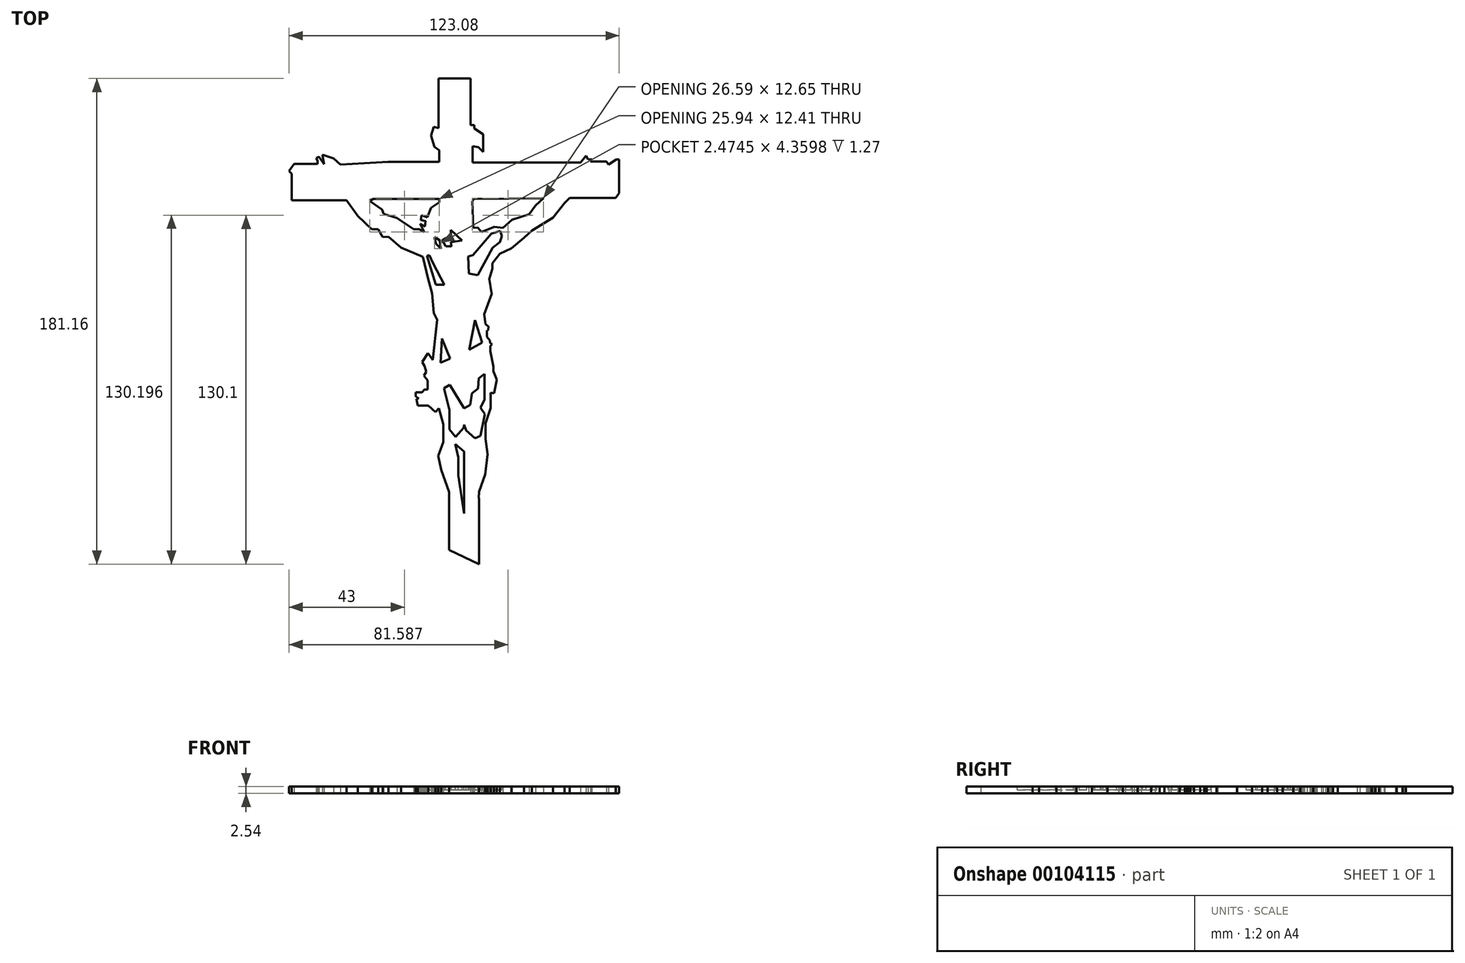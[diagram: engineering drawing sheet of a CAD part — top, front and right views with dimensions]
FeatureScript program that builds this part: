
annotation { "Feature Type Name" : "Feature", "Feature Type Description" : "" }
export const myFeature = defineFeature(function(context is Context, id is Id, definition is map)
    precondition{}
    {
        {
            var Q0;
            Q0=qCreatedBy(makeId("Top.planeOp"),FACE);
            var sketch = newSketch(context, id + "F0", { "sketchPlane" : qUnion([Q0])});
            skLineSegment(sketch, "E0", {"start": v(-9.57, 83.57) * mm, "end": v(-6, 83.57) * mm});
            skLineSegment(sketch, "E1", {"start": v(-6, 83.57) * mm, "end": v(-2.71, 83.57) * mm});
            skLineSegment(sketch, "E2", {"start": v(-2.71, 83.57) * mm, "end": v(1.86, 83.57) * mm});
            skLineSegment(sketch, "E3", {"start": v(1.86, 83.57) * mm, "end": v(2.48, 83.57) * mm});
            skLineSegment(sketch, "E4", {"start": v(2.48, 83.57) * mm, "end": v(2.48, 74.86) * mm});
            skLineSegment(sketch, "E5", {"start": v(2.48, 74.86) * mm, "end": v(2.48, 66.25) * mm});
            skLineSegment(sketch, "E6", {"start": v(2.48, 66.25) * mm, "end": v(3.84, 66.25) * mm});
            skLineSegment(sketch, "E7", {"start": v(3.14, 58.38) * mm, "end": v(3.14, 52.19) * mm});
            skLineSegment(sketch, "E8", {"start": v(3.14, 52.19) * mm, "end": v(24.8, 52.19) * mm});
            skLineSegment(sketch, "E9", {"start": v(24.8, 52.19) * mm, "end": v(43.45, 52.19) * mm});
            skLineSegment(sketch, "E10", {"start": v(47.37, 52.57) * mm, "end": v(53.14, 52.57) * mm});
            skLineSegment(sketch, "E11", {"start": v(53.14, 52.57) * mm, "end": v(53.88, 51.45) * mm});
            skLineSegment(sketch, "E12", {"start": v(53.88, 51.45) * mm, "end": v(56.77, 53.38) * mm});
            skLineSegment(sketch, "E13", {"start": v(56.77, 53.38) * mm, "end": v(57.85, 53.38) * mm});
            skLineSegment(sketch, "E14", {"start": v(57.85, 53.38) * mm, "end": v(57.85, 40.79) * mm});
            skLineSegment(sketch, "E15", {"start": v(57.85, 40.79) * mm, "end": v(56.55, 38.99) * mm});
            skLineSegment(sketch, "E16", {"start": v(56.55, 38.99) * mm, "end": v(39.44, 38.99) * mm});
            skLineSegment(sketch, "E17", {"start": v(29.65, 38.93) * mm, "end": v(3.69, 38.7) * mm});
            skLineSegment(sketch, "E18", {"start": v(3.69, 38.7) * mm, "end": v(3.06, 37.74) * mm});
            skLineSegment(sketch, "E19", {"start": v(3.06, 37.74) * mm, "end": v(3.47, 27.88) * mm});
            skLineSegment(sketch, "E20", {"start": v(3.47, 27.88) * mm, "end": v(5.04, 27.94) * mm});
            skLineSegment(sketch, "E21", {"start": v(5.04, 27.94) * mm, "end": v(6.46, 26.28) * mm});
            skLineSegment(sketch, "E22", {"start": v(6.46, 26.28) * mm, "end": v(11.34, 28.3) * mm});
            skLineSegment(sketch, "E23", {"start": v(11.34, 28.3) * mm, "end": v(14.45, 27.88) * mm});
            skLineSegment(sketch, "E24", {"start": v(14.45, 27.88) * mm, "end": v(17.99, 30.92) * mm});
            skLineSegment(sketch, "E25", {"start": v(17.99, 30.92) * mm, "end": v(24.26, 32.96) * mm});
            skLineSegment(sketch, "E26", {"start": v(24.26, 32.96) * mm, "end": v(26.65, 36.24) * mm});
            skLineSegment(sketch, "E27", {"start": v(26.65, 36.24) * mm, "end": v(29.65, 38.93) * mm});
            skLineSegment(sketch, "E28", {"start": v(39.44, 38.99) * mm, "end": v(37.47, 37.1) * mm});
            skLineSegment(sketch, "E29", {"start": v(37.47, 37.1) * mm, "end": v(33.12, 31.64) * mm});
            skLineSegment(sketch, "E30", {"start": v(33.12, 31.64) * mm, "end": v(25.33, 26.87) * mm});
            skLineSegment(sketch, "E31", {"start": v(25.33, 26.87) * mm, "end": v(22.33, 24.19) * mm});
            skLineSegment(sketch, "E32", {"start": v(22.33, 24.19) * mm, "end": v(17.66, 20.26) * mm});
            skLineSegment(sketch, "E33", {"start": v(17.66, 20.26) * mm, "end": v(13.41, 18.17) * mm});
            skLineSegment(sketch, "E34", {"start": v(13.41, 18.17) * mm, "end": v(10.56, 14.7) * mm});
            skLineSegment(sketch, "E35", {"start": v(10.56, 14.7) * mm, "end": v(10.56, 12.67) * mm});
            skLineSegment(sketch, "E36", {"start": v(10.56, 12.67) * mm, "end": v(9.45, 8.78) * mm});
            skLineSegment(sketch, "E37", {"start": v(9.45, 8.78) * mm, "end": v(10.35, 3.2) * mm});
            skLineSegment(sketch, "E38", {"start": v(10.35, 3.2) * mm, "end": v(7.5, -4.35) * mm});
            skLineSegment(sketch, "E39", {"start": v(7.5, -4.35) * mm, "end": v(8, -8.1) * mm});
            skLineSegment(sketch, "E40", {"start": v(8, -8.1) * mm, "end": v(9.18, -9.02) * mm});
            skLineSegment(sketch, "E41", {"start": v(9.18, -9.02) * mm, "end": v(8.97, -10.46) * mm});
            skLineSegment(sketch, "E42", {"start": v(8.97, -10.46) * mm, "end": v(8.53, -10.4) * mm});
            skLineSegment(sketch, "E43", {"start": v(8.53, -10.4) * mm, "end": v(8.53, -12.78) * mm});
            skLineSegment(sketch, "E44", {"start": v(8.53, -12.78) * mm, "end": v(9.67, -14.22) * mm});
            skLineSegment(sketch, "E45", {"start": v(9.67, -14.22) * mm, "end": v(9.67, -14.96) * mm});
            skLineSegment(sketch, "E46", {"start": v(9.67, -14.96) * mm, "end": v(10.4, -15.53) * mm});
            skLineSegment(sketch, "E47", {"start": v(10.4, -15.53) * mm, "end": v(9.86, -16.26) * mm});
            skLineSegment(sketch, "E48", {"start": v(9.86, -16.26) * mm, "end": v(9.86, -18.07) * mm});
            skLineSegment(sketch, "E49", {"start": v(9.86, -18.07) * mm, "end": v(11, -23.8) * mm});
            skLineSegment(sketch, "E50", {"start": v(11, -23.8) * mm, "end": v(11, -25.56) * mm});
            skLineSegment(sketch, "E51", {"start": v(11, -25.56) * mm, "end": v(12.16, -28.82) * mm});
            skLineSegment(sketch, "E52", {"start": v(12.16, -28.82) * mm, "end": v(11.23, -33.84) * mm});
            skLineSegment(sketch, "E53", {"start": v(11.23, -33.84) * mm, "end": v(9.94, -33.6) * mm});
            skLineSegment(sketch, "E54", {"start": v(9.94, -33.6) * mm, "end": v(9.94, -39.35) * mm});
            skLineSegment(sketch, "E55", {"start": v(9.94, -39.35) * mm, "end": v(7.96, -45) * mm});
            skLineSegment(sketch, "E56", {"start": v(7.96, -45) * mm, "end": v(7.96, -50.93) * mm});
            skLineSegment(sketch, "E57", {"start": v(7.96, -50.93) * mm, "end": v(8.79, -56.57) * mm});
            skLineSegment(sketch, "E58", {"start": v(8.79, -56.57) * mm, "end": v(7.88, -64.13) * mm});
            skLineSegment(sketch, "E59", {"start": v(7.88, -64.13) * mm, "end": v(5.56, -70.58) * mm});
            skLineSegment(sketch, "E60", {"start": v(5.56, -70.58) * mm, "end": v(5.46, -73) * mm});
            skLineSegment(sketch, "E61", {"start": v(5.46, -73) * mm, "end": v(5.67, -73) * mm});
            skLineSegment(sketch, "E62", {"start": v(5.67, -73) * mm, "end": v(5.67, -97.59) * mm});
            skLineSegment(sketch, "E63", {"start": v(5.67, -97.59) * mm, "end": v(-5.6, -92.27) * mm});
            skLineSegment(sketch, "E64", {"start": v(-5.6, -92.27) * mm, "end": v(-5.6, -70.66) * mm});
            skLineSegment(sketch, "E65", {"start": v(-5.6, -70.66) * mm, "end": v(-8.45, -62.4) * mm});
            skLineSegment(sketch, "E66", {"start": v(-8.45, -62.4) * mm, "end": v(-9.66, -57.29) * mm});
            skLineSegment(sketch, "E67", {"start": v(-9.66, -57.29) * mm, "end": v(-7.75, -52.08) * mm});
            skLineSegment(sketch, "E68", {"start": v(-7.75, -52.08) * mm, "end": v(-7.75, -45.4) * mm});
            skLineSegment(sketch, "E69", {"start": v(-7.75, -45.4) * mm, "end": v(-9.32, -39.5) * mm});
            skLineSegment(sketch, "E70", {"start": v(-9.32, -39.5) * mm, "end": v(-10.62, -40.88) * mm});
            skLineSegment(sketch, "E71", {"start": v(-10.62, -40.88) * mm, "end": v(-13.3, -38.37) * mm});
            skLineSegment(sketch, "E72", {"start": v(-13.3, -38.37) * mm, "end": v(-17.22, -38.37) * mm});
            skLineSegment(sketch, "E73", {"start": v(-17.22, -38.37) * mm, "end": v(-17.74, -35.93) * mm});
            skLineSegment(sketch, "E74", {"start": v(-17.74, -35.93) * mm, "end": v(-16.9, -35.76) * mm});
            skLineSegment(sketch, "E75", {"start": v(-16.9, -35.76) * mm, "end": v(-17.97, -34.99) * mm});
            skLineSegment(sketch, "E76", {"start": v(-17.97, -34.99) * mm, "end": v(-17.97, -33.43) * mm});
            skLineSegment(sketch, "E77", {"start": v(-17.97, -33.43) * mm, "end": v(-15.56, -33.43) * mm});
            skLineSegment(sketch, "E78", {"start": v(-15.56, -33.43) * mm, "end": v(-14.8, -32.43) * mm});
            skLineSegment(sketch, "E79", {"start": v(-14.8, -32.43) * mm, "end": v(-13.6, -32.43) * mm});
            skLineSegment(sketch, "E80", {"start": v(-13.6, -32.43) * mm, "end": v(-13.6, -29.02) * mm});
            skLineSegment(sketch, "E81", {"start": v(-13.6, -29.02) * mm, "end": v(-14.9, -27.21) * mm});
            skLineSegment(sketch, "E82", {"start": v(-14.9, -27.21) * mm, "end": v(-14.05, -25.9) * mm});
            skLineSegment(sketch, "E83", {"start": v(-14.05, -25.9) * mm, "end": v(-14.65, -23.75) * mm});
            skLineSegment(sketch, "E84", {"start": v(-14.65, -23.75) * mm, "end": v(-15.64, -22.18) * mm});
            skLineSegment(sketch, "E85", {"start": v(-15.64, -22.18) * mm, "end": v(-13.48, -18.84) * mm});
            skLineSegment(sketch, "E86", {"start": v(-13.48, -18.84) * mm, "end": v(-11.66, -21.36) * mm});
            skLineSegment(sketch, "E87", {"start": v(-11.66, -21.36) * mm, "end": v(-9.97, -6.45) * mm});
            skLineSegment(sketch, "E88", {"start": v(-9.97, -6.45) * mm, "end": v(-11.24, -3.85) * mm});
            skLineSegment(sketch, "E89", {"start": v(-11.24, -3.85) * mm, "end": v(-11.94, 3.5) * mm});
            skLineSegment(sketch, "E90", {"start": v(-11.94, 3.5) * mm, "end": v(-13.4, 9.05) * mm});
            skLineSegment(sketch, "E91", {"start": v(-13.4, 9.05) * mm, "end": v(-15.38, 17.04) * mm});
            skLineSegment(sketch, "E92", {"start": v(-15.38, 17.04) * mm, "end": v(-23.43, 20.56) * mm});
            skLineSegment(sketch, "E93", {"start": v(-23.43, 20.56) * mm, "end": v(-28.2, 24.55) * mm});
            skLineSegment(sketch, "E94", {"start": v(-28.2, 24.55) * mm, "end": v(-30.3, 24.4) * mm});
            skLineSegment(sketch, "E95", {"start": v(-30.3, 24.4) * mm, "end": v(-31.94, 27.36) * mm});
            skLineSegment(sketch, "E96", {"start": v(-31.94, 27.36) * mm, "end": v(-34.37, 27.36) * mm});
            skLineSegment(sketch, "E97", {"start": v(-34.37, 27.36) * mm, "end": v(-39.56, 32.31) * mm});
            skLineSegment(sketch, "E98", {"start": v(-39.56, 32.31) * mm, "end": v(-43.77, 38.1) * mm});
            skLineSegment(sketch, "E99", {"start": v(-43.77, 38.1) * mm, "end": v(-64.18, 38.1) * mm});
            skLineSegment(sketch, "E100", {"start": v(-64.18, 38.1) * mm, "end": v(-64.18, 48) * mm});
            skLineSegment(sketch, "E101", {"start": v(-64.18, 48) * mm, "end": v(-65.23, 49.02) * mm});
            skLineSegment(sketch, "E102", {"start": v(-65.23, 49.02) * mm, "end": v(-63.4, 51.74) * mm});
            skLineSegment(sketch, "E103", {"start": v(-63.4, 51.74) * mm, "end": v(-54.56, 51.74) * mm});
            skLineSegment(sketch, "E104", {"start": v(-54.56, 51.74) * mm, "end": v(-54.56, 52.76) * mm});
            skLineSegment(sketch, "E105", {"start": v(-54.56, 52.76) * mm, "end": v(-55.1, 53.85) * mm});
            skLineSegment(sketch, "E106", {"start": v(-55.1, 53.85) * mm, "end": v(-54.07, 54.37) * mm});
            skLineSegment(sketch, "E107", {"start": v(-54.07, 54.37) * mm, "end": v(-52.11, 51.6) * mm});
            skLineSegment(sketch, "E108", {"start": v(-52.11, 51.6) * mm, "end": v(-52.86, 55.14) * mm});
            skLineSegment(sketch, "E109", {"start": v(-52.86, 55.14) * mm, "end": v(-48.58, 53.71) * mm});
            skLineSegment(sketch, "E110", {"start": v(-48.58, 53.71) * mm, "end": v(-46.13, 51.54) * mm});
            skLineSegment(sketch, "E111", {"start": v(-46.13, 51.54) * mm, "end": v(-28.25, 52.5) * mm});
            skLineSegment(sketch, "E112", {"start": v(-28.25, 52.5) * mm, "end": v(-9.2, 52.5) * mm});
            skLineSegment(sketch, "E113", {"start": v(-9.2, 52.5) * mm, "end": v(-9.2, 56.87) * mm});
            skLineSegment(sketch, "E114", {"start": v(-9.2, 56.87) * mm, "end": v(-10.99, 58.11) * mm});
            skLineSegment(sketch, "E115", {"start": v(-10.99, 58.11) * mm, "end": v(-12.32, 62.3) * mm});
            skLineSegment(sketch, "E116", {"start": v(-12.32, 62.3) * mm, "end": v(-11.26, 65.6) * mm});
            skLineSegment(sketch, "E117", {"start": v(-11.26, 65.6) * mm, "end": v(-9.56, 65.04) * mm});
            skLineSegment(sketch, "E118", {"start": v(-9.56, 65.04) * mm, "end": v(-9.57, 83.57) * mm});
            skLineSegment(sketch, "E119", {"start": v(3.84, 66.25) * mm, "end": v(3.84, 64.97) * mm});
            skLineSegment(sketch, "E120", {"start": v(3.84, 64.97) * mm, "end": v(7.17, 62.83) * mm});
            skLineSegment(sketch, "E121", {"start": v(7.17, 62.83) * mm, "end": v(7.17, 56.25) * mm});
            skLineSegment(sketch, "E122", {"start": v(7.17, 56.25) * mm, "end": v(5.3, 58.03) * mm});
            skLineSegment(sketch, "E123", {"start": v(5.3, 58.03) * mm, "end": v(3.14, 58.38) * mm});
            skLineSegment(sketch, "E124", {"start": v(-9.26, 38.71) * mm, "end": v(-9.26, 37.43) * mm});
            skLineSegment(sketch, "E125", {"start": v(-9.26, 37.43) * mm, "end": v(-12.3, 35.35) * mm});
            skLineSegment(sketch, "E126", {"start": v(-12.3, 35.35) * mm, "end": v(-13.74, 31.75) * mm});
            skLineSegment(sketch, "E127", {"start": v(-13.74, 31.75) * mm, "end": v(-15.91, 32.62) * mm});
            skLineSegment(sketch, "E128", {"start": v(-15.91, 32.62) * mm, "end": v(-16.07, 30.79) * mm});
            skLineSegment(sketch, "E129", {"start": v(-16.07, 30.79) * mm, "end": v(-14.38, 30.39) * mm});
            skLineSegment(sketch, "E130", {"start": v(-14.38, 30.39) * mm, "end": v(-14.62, 28.39) * mm});
            skLineSegment(sketch, "E131", {"start": v(-14.62, 28.39) * mm, "end": v(-16.39, 29.43) * mm});
            skLineSegment(sketch, "E132", {"start": v(-16.39, 29.43) * mm, "end": v(-14.78, 26.3) * mm});
            skLineSegment(sketch, "E133", {"start": v(-14.78, 26.3) * mm, "end": v(-16.79, 27.35) * mm});
            skLineSegment(sketch, "E134", {"start": v(-16.79, 27.35) * mm, "end": v(-18.79, 27.35) * mm});
            skLineSegment(sketch, "E135", {"start": v(-18.79, 27.35) * mm, "end": v(-25.03, 31.5) * mm});
            skLineSegment(sketch, "E136", {"start": v(-25.03, 31.5) * mm, "end": v(-30, 33.03) * mm});
            skLineSegment(sketch, "E137", {"start": v(-30, 33.03) * mm, "end": v(-30.64, 34.71) * mm});
            skLineSegment(sketch, "E138", {"start": v(-30.64, 34.71) * mm, "end": v(-35.2, 37.83) * mm});
            skLineSegment(sketch, "E139", {"start": v(-35.2, 37.83) * mm, "end": v(-33.92, 38.63) * mm});
            skLineSegment(sketch, "E140", {"start": v(-33.92, 38.63) * mm, "end": v(-9.26, 38.71) * mm});
            skLineSegment(sketch, "E141", {"start": v(43.45, 52.19) * mm, "end": v(45.43, 54.8) * mm});
            skLineSegment(sketch, "E142", {"start": v(45.43, 54.8) * mm, "end": v(46.3, 53.38) * mm});
            skLineSegment(sketch, "E143", {"start": v(46.3, 53.38) * mm, "end": v(47.6, 53.46) * mm});
            skLineSegment(sketch, "E144", {"start": v(47.6, 53.46) * mm, "end": v(47.1, 52.7) * mm});
            skLineSegment(sketch, "E145", {"start": v(47.1, 52.7) * mm, "end": v(47.37, 52.57) * mm});
            skSolve(sketch);
        }
        {
            var Q0;
            Q0 = qSketchRegion(id + "F0", true);
            extrude(context, id + "F1", {"entities" : qUnion([Q0]), "depth" : 2.54 * mm});
        }
        {
            var Q0;
            Q0=makeQuery(id+"F1.opExtrude","CAP_FACE",FACE,{"disambiguationData":[OSD([sQuery(id+"F0.wireOp",EDGE,"E0"),sQuery(id+"F0.wireOp",EDGE,"E1"),sQuery(id+"F0.wireOp",EDGE,"E2"),sQuery(id+"F0.wireOp",EDGE,"E3"),sQuery(id+"F0.wireOp",EDGE,"E4"),sQuery(id+"F0.wireOp",EDGE,"E5"),sQuery(id+"F0.wireOp",EDGE,"E6"),sQuery(id+"F0.wireOp",EDGE,"E7"),sQuery(id+"F0.wireOp",EDGE,"E8"),sQuery(id+"F0.wireOp",EDGE,"E9"),sQuery(id+"F0.wireOp",EDGE,"E10"),sQuery(id+"F0.wireOp",EDGE,"E11"),sQuery(id+"F0.wireOp",EDGE,"E12"),sQuery(id+"F0.wireOp",EDGE,"E13"),sQuery(id+"F0.wireOp",EDGE,"E14"),sQuery(id+"F0.wireOp",EDGE,"E15"),sQuery(id+"F0.wireOp",EDGE,"E16"),sQuery(id+"F0.wireOp",EDGE,"E17"),sQuery(id+"F0.wireOp",EDGE,"E18"),sQuery(id+"F0.wireOp",EDGE,"E19"),sQuery(id+"F0.wireOp",EDGE,"E20"),sQuery(id+"F0.wireOp",EDGE,"E21"),sQuery(id+"F0.wireOp",EDGE,"E22"),sQuery(id+"F0.wireOp",EDGE,"E23"),sQuery(id+"F0.wireOp",EDGE,"E24"),sQuery(id+"F0.wireOp",EDGE,"E25"),sQuery(id+"F0.wireOp",EDGE,"E26"),sQuery(id+"F0.wireOp",EDGE,"E27"),sQuery(id+"F0.wireOp",EDGE,"E28"),sQuery(id+"F0.wireOp",EDGE,"E29"),sQuery(id+"F0.wireOp",EDGE,"E30"),sQuery(id+"F0.wireOp",EDGE,"E31"),sQuery(id+"F0.wireOp",EDGE,"E32"),sQuery(id+"F0.wireOp",EDGE,"E33"),sQuery(id+"F0.wireOp",EDGE,"E34"),sQuery(id+"F0.wireOp",EDGE,"E35"),sQuery(id+"F0.wireOp",EDGE,"E36"),sQuery(id+"F0.wireOp",EDGE,"E37"),sQuery(id+"F0.wireOp",EDGE,"E38"),sQuery(id+"F0.wireOp",EDGE,"E39"),sQuery(id+"F0.wireOp",EDGE,"E40"),sQuery(id+"F0.wireOp",EDGE,"E41"),sQuery(id+"F0.wireOp",EDGE,"E42"),sQuery(id+"F0.wireOp",EDGE,"E43"),sQuery(id+"F0.wireOp",EDGE,"E44"),sQuery(id+"F0.wireOp",EDGE,"E45"),sQuery(id+"F0.wireOp",EDGE,"E46"),sQuery(id+"F0.wireOp",EDGE,"E47"),sQuery(id+"F0.wireOp",EDGE,"E48"),sQuery(id+"F0.wireOp",EDGE,"E49"),sQuery(id+"F0.wireOp",EDGE,"E50"),sQuery(id+"F0.wireOp",EDGE,"E51"),sQuery(id+"F0.wireOp",EDGE,"E52"),sQuery(id+"F0.wireOp",EDGE,"E53"),sQuery(id+"F0.wireOp",EDGE,"E54"),sQuery(id+"F0.wireOp",EDGE,"E55"),sQuery(id+"F0.wireOp",EDGE,"E56"),sQuery(id+"F0.wireOp",EDGE,"E57"),sQuery(id+"F0.wireOp",EDGE,"E58"),sQuery(id+"F0.wireOp",EDGE,"E59"),sQuery(id+"F0.wireOp",EDGE,"E60"),sQuery(id+"F0.wireOp",EDGE,"E61"),sQuery(id+"F0.wireOp",EDGE,"E62"),sQuery(id+"F0.wireOp",EDGE,"E63"),sQuery(id+"F0.wireOp",EDGE,"E64"),sQuery(id+"F0.wireOp",EDGE,"E65"),sQuery(id+"F0.wireOp",EDGE,"E66"),sQuery(id+"F0.wireOp",EDGE,"E67"),sQuery(id+"F0.wireOp",EDGE,"E68"),sQuery(id+"F0.wireOp",EDGE,"E69"),sQuery(id+"F0.wireOp",EDGE,"E70"),sQuery(id+"F0.wireOp",EDGE,"E71"),sQuery(id+"F0.wireOp",EDGE,"E72"),sQuery(id+"F0.wireOp",EDGE,"E73"),sQuery(id+"F0.wireOp",EDGE,"E74"),sQuery(id+"F0.wireOp",EDGE,"E75"),sQuery(id+"F0.wireOp",EDGE,"E76"),sQuery(id+"F0.wireOp",EDGE,"E77"),sQuery(id+"F0.wireOp",EDGE,"E78"),sQuery(id+"F0.wireOp",EDGE,"E79"),sQuery(id+"F0.wireOp",EDGE,"E80"),sQuery(id+"F0.wireOp",EDGE,"E81"),sQuery(id+"F0.wireOp",EDGE,"E82"),sQuery(id+"F0.wireOp",EDGE,"E83"),sQuery(id+"F0.wireOp",EDGE,"E84"),sQuery(id+"F0.wireOp",EDGE,"E85"),sQuery(id+"F0.wireOp",EDGE,"E86"),sQuery(id+"F0.wireOp",EDGE,"E87"),sQuery(id+"F0.wireOp",EDGE,"E88"),sQuery(id+"F0.wireOp",EDGE,"E89"),sQuery(id+"F0.wireOp",EDGE,"E90"),sQuery(id+"F0.wireOp",EDGE,"E91"),sQuery(id+"F0.wireOp",EDGE,"E92"),sQuery(id+"F0.wireOp",EDGE,"E93"),sQuery(id+"F0.wireOp",EDGE,"E94"),sQuery(id+"F0.wireOp",EDGE,"E95"),sQuery(id+"F0.wireOp",EDGE,"E96"),sQuery(id+"F0.wireOp",EDGE,"E97"),sQuery(id+"F0.wireOp",EDGE,"E98"),sQuery(id+"F0.wireOp",EDGE,"E99"),sQuery(id+"F0.wireOp",EDGE,"E100"),sQuery(id+"F0.wireOp",EDGE,"E101"),sQuery(id+"F0.wireOp",EDGE,"E102"),sQuery(id+"F0.wireOp",EDGE,"E103"),sQuery(id+"F0.wireOp",EDGE,"E104"),sQuery(id+"F0.wireOp",EDGE,"E105"),sQuery(id+"F0.wireOp",EDGE,"E106"),sQuery(id+"F0.wireOp",EDGE,"E107"),sQuery(id+"F0.wireOp",EDGE,"E108"),sQuery(id+"F0.wireOp",EDGE,"E109"),sQuery(id+"F0.wireOp",EDGE,"E110"),sQuery(id+"F0.wireOp",EDGE,"E111"),sQuery(id+"F0.wireOp",EDGE,"E112"),sQuery(id+"F0.wireOp",EDGE,"E113"),sQuery(id+"F0.wireOp",EDGE,"E114"),sQuery(id+"F0.wireOp",EDGE,"E115"),sQuery(id+"F0.wireOp",EDGE,"E116"),sQuery(id+"F0.wireOp",EDGE,"E117"),sQuery(id+"F0.wireOp",EDGE,"E118"),sQuery(id+"F0.wireOp",EDGE,"E119"),sQuery(id+"F0.wireOp",EDGE,"E120"),sQuery(id+"F0.wireOp",EDGE,"E121"),sQuery(id+"F0.wireOp",EDGE,"E122"),sQuery(id+"F0.wireOp",EDGE,"E123"),sQuery(id+"F0.wireOp",EDGE,"E124"),sQuery(id+"F0.wireOp",EDGE,"E125"),sQuery(id+"F0.wireOp",EDGE,"E126"),sQuery(id+"F0.wireOp",EDGE,"E127"),sQuery(id+"F0.wireOp",EDGE,"E128"),sQuery(id+"F0.wireOp",EDGE,"E129"),sQuery(id+"F0.wireOp",EDGE,"E130"),sQuery(id+"F0.wireOp",EDGE,"E131"),sQuery(id+"F0.wireOp",EDGE,"E132"),sQuery(id+"F0.wireOp",EDGE,"E133"),sQuery(id+"F0.wireOp",EDGE,"E134"),sQuery(id+"F0.wireOp",EDGE,"E135"),sQuery(id+"F0.wireOp",EDGE,"E136"),sQuery(id+"F0.wireOp",EDGE,"E137"),sQuery(id+"F0.wireOp",EDGE,"E138"),sQuery(id+"F0.wireOp",EDGE,"E139"),sQuery(id+"F0.wireOp",EDGE,"E140"),sQuery(id+"F0.wireOp",EDGE,"E141"),sQuery(id+"F0.wireOp",EDGE,"E142"),sQuery(id+"F0.wireOp",EDGE,"E143"),sQuery(id+"F0.wireOp",EDGE,"E144"),sQuery(id+"F0.wireOp",EDGE,"E145")])],"isStart":false});
            var sketch = newSketch(context, id + "F2", { "sketchPlane" : qUnion([Q0])});
            skLineSegment(sketch, "E146", {"start": v(-6.92, 24.07) * mm, "end": v(-4.85, 24.08) * mm});
            skLineSegment(sketch, "E147", {"start": v(-4.85, 24.08) * mm, "end": v(-4.86, 27.16) * mm});
            skLineSegment(sketch, "E148", {"start": v(-4.86, 27.16) * mm, "end": v(-0.73, 23.23) * mm});
            skLineSegment(sketch, "E149", {"start": v(-0.73, 23.23) * mm, "end": v(-4.9, 22.51) * mm});
            skLineSegment(sketch, "E150", {"start": v(-4.9, 22.51) * mm, "end": v(-4.65, 20.99) * mm});
            skLineSegment(sketch, "E151", {"start": v(-4.65, 20.99) * mm, "end": v(-6.88, 20.99) * mm});
            skLineSegment(sketch, "E152", {"start": v(-6.88, 20.99) * mm, "end": v(-8.1, 23.32) * mm});
            skLineSegment(sketch, "E153", {"start": v(-8.1, 23.32) * mm, "end": v(-6.92, 24.07) * mm});
            skLineSegment(sketch, "E154", {"start": v(-11.05, 24.44) * mm, "end": v(-9.1, 23.26) * mm});
            skLineSegment(sketch, "E155", {"start": v(-9.1, 23.26) * mm, "end": v(-8.58, 20.08) * mm});
            skLineSegment(sketch, "E156", {"start": v(-8.58, 20.08) * mm, "end": v(-10.52, 22.02) * mm});
            skLineSegment(sketch, "E157", {"start": v(-10.52, 22.02) * mm, "end": v(-11.05, 24.44) * mm});
            skLineSegment(sketch, "E158", {"start": v(1.52, 17.17) * mm, "end": v(3.34, 17.72) * mm});
            skLineSegment(sketch, "E159", {"start": v(3.34, 17.72) * mm, "end": v(10.2, 25.67) * mm});
            skLineSegment(sketch, "E160", {"start": v(10.2, 25.67) * mm, "end": v(13.49, 26.77) * mm});
            skLineSegment(sketch, "E161", {"start": v(13.49, 26.77) * mm, "end": v(14.13, 24.83) * mm});
            skLineSegment(sketch, "E162", {"start": v(14.13, 24.83) * mm, "end": v(13.36, 22.57) * mm});
            skLineSegment(sketch, "E163", {"start": v(13.36, 22.57) * mm, "end": v(10.75, 20.5) * mm});
            skLineSegment(sketch, "E164", {"start": v(10.75, 20.5) * mm, "end": v(5.17, 10.19) * mm});
            skLineSegment(sketch, "E165", {"start": v(5.17, 10.19) * mm, "end": v(1.76, 10.85) * mm});
            skLineSegment(sketch, "E166", {"start": v(1.76, 10.85) * mm, "end": v(1.52, 17.17) * mm});
            skLineSegment(sketch, "E167", {"start": v(-13.78, 17.41) * mm, "end": v(-10.49, 6.63) * mm});
            skLineSegment(sketch, "E168", {"start": v(-10.49, 6.63) * mm, "end": v(-7.35, 6.63) * mm});
            skLineSegment(sketch, "E169", {"start": v(-7.35, 6.63) * mm, "end": v(-11.47, 14.68) * mm});
            skLineSegment(sketch, "E170", {"start": v(-11.47, 14.68) * mm, "end": v(-12.93, 17.72) * mm});
            skLineSegment(sketch, "E171", {"start": v(-12.93, 17.72) * mm, "end": v(-13.78, 17.41) * mm});
            skLineSegment(sketch, "E172", {"start": v(-8.25, -13.37) * mm, "end": v(-5.12, -20.9) * mm});
            skLineSegment(sketch, "E173", {"start": v(-5.12, -20.9) * mm, "end": v(-8.68, -22.38) * mm});
            skLineSegment(sketch, "E174", {"start": v(-8.68, -22.38) * mm, "end": v(-8.25, -13.37) * mm});
            skLineSegment(sketch, "E175", {"start": v(4.03, -6.53) * mm, "end": v(1.95, -17.55) * mm});
            skLineSegment(sketch, "E176", {"start": v(1.95, -17.55) * mm, "end": v(6.82, -14.88) * mm});
            skLineSegment(sketch, "E177", {"start": v(6.82, -14.88) * mm, "end": v(4.03, -6.53) * mm});
            skLineSegment(sketch, "E178", {"start": v(-5.29, -30.72) * mm, "end": v(0, -39.5) * mm});
            skPoint(sketch, "E178.startSnap0", {"position": v(-13.6, -30.72) * mm});
            skLineSegment(sketch, "E179", {"start": v(-0.1, -46.72) * mm, "end": v(-3.1, -50.11) * mm});
            skLineSegment(sketch, "E180", {"start": v(-3.1, -50.11) * mm, "end": v(-5.48, -47.32) * mm});
            skLineSegment(sketch, "E181", {"start": v(-5.48, -47.32) * mm, "end": v(-5.48, -40.14) * mm});
            skLineSegment(sketch, "E182", {"start": v(-5.48, -40.14) * mm, "end": v(-7.48, -31.96) * mm});
            skLineSegment(sketch, "E183", {"start": v(-7.48, -31.96) * mm, "end": v(-5.29, -30.72) * mm});
            skLineSegment(sketch, "E184", {"start": v(0, -39.5) * mm, "end": v(2.29, -38.12) * mm});
            skLineSegment(sketch, "E185", {"start": v(2.29, -38.12) * mm, "end": v(2.97, -33.9) * mm});
            skLineSegment(sketch, "E186", {"start": v(2.97, -33.9) * mm, "end": v(5.28, -32.12) * mm});
            skLineSegment(sketch, "E187", {"start": v(5.28, -32.12) * mm, "end": v(5.52, -28.26) * mm});
            skLineSegment(sketch, "E188", {"start": v(5.52, -28.26) * mm, "end": v(7.6, -26.64) * mm});
            skLineSegment(sketch, "E189", {"start": v(7.6, -26.64) * mm, "end": v(7.6, -36.3) * mm});
            skLineSegment(sketch, "E190", {"start": v(7.6, -36.3) * mm, "end": v(6.06, -39.23) * mm});
            skLineSegment(sketch, "E191", {"start": v(6.06, -39.23) * mm, "end": v(7.76, -41.55) * mm});
            skLineSegment(sketch, "E192", {"start": v(7.76, -41.55) * mm, "end": v(6.13, -49.73) * mm});
            skLineSegment(sketch, "E193", {"start": v(6.13, -49.73) * mm, "end": v(4.05, -50.66) * mm});
            skLineSegment(sketch, "E194", {"start": v(4.05, -50.66) * mm, "end": v(0.8, -47.65) * mm});
            skLineSegment(sketch, "E195", {"start": v(0.8, -47.65) * mm, "end": v(0, -45.48) * mm});
            skLineSegment(sketch, "E196", {"start": v(0, -45.48) * mm, "end": v(-0.1, -46.72) * mm});
            skLineSegment(sketch, "E197", {"start": v(-3.24, -52.8) * mm, "end": v(-2.08, -57.7) * mm});
            skLineSegment(sketch, "E198", {"start": v(-2.08, -57.7) * mm, "end": v(-2.08, -64.51) * mm});
            skLineSegment(sketch, "E199", {"start": v(-2.08, -64.51) * mm, "end": v(0, -78.65) * mm});
            skLineSegment(sketch, "E200", {"start": v(0, -78.65) * mm, "end": v(0, -66.23) * mm});
            skLineSegment(sketch, "E201", {"start": v(0, -66.23) * mm, "end": v(0, -55.52) * mm});
            skLineSegment(sketch, "E202", {"start": v(0, -55.52) * mm, "end": v(-3.24, -52.8) * mm});
            skSolve(sketch);
        }
        {
            var Q0;
            Q0 = qSketchRegion(id + "F2", true);
            extrude(context, id + "F3", {"entities" : qUnion([Q0]), "operationType" : NewBodyOperationType.REMOVE, "oppositeDirection" : true, "depth" : 1.27 * mm});
        }
    });
